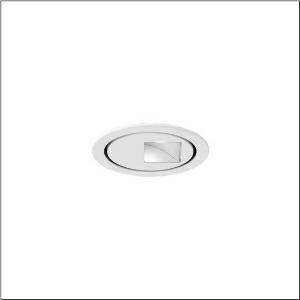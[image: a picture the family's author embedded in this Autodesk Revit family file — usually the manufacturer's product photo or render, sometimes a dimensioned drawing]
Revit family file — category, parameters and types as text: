
# Revit family: lunis_11_micro_round_51dj11b71wf21
name_source: partatom
category: Lighting Fixtures
units: mm (PartAtom-declared; Revit-internal decimal feet)

## family parameters
Cut with Voids When Loaded = No
Host = Face
Light Source = No
Part Type = Normal
Room Calculation Point = No
Round Connector Dimension = Use Diameter
Shared = No

## types (1)
- Lunis 11 micro round (1 x LED 3000K / CRI = 80 (unbekannt), 1320 lm, 3000K)
    Apparent Load = 20 VA
    CIE Flux Codes = 42 75 96 100 100
    Color Rendering = 80
    Color Temperature = 3000K
    Default Elevation = 1800 mm
    Description = Lunis 11 micro round, downlight, light control with wallwasher, of highly reflective aluminium, highly specular, light emission: direct distribution, LED rated luminous flux: 1.320lm, light colour: 830, control gear: ECG, with terminal, 3-pole, mains connection: 220..230V, AC/DC, 0/50..60Hz, LED module, luminaire module, of aluminium, highly specular, white, diameter: 114mm, clamping range: 1..40mm, recessing ring, of plastic, traffic white (RAL 9016), protection rating (complete): IP20, insulation class (complete): insulation class II (safety insulation), certification: CE, permissible ambient temperature for indoor applications: 0..+35°C, packaging unit: 1 piece
    Height = 0 mm  [stored 0 ft]
    Lamp = 1 x LED 3000K / CRI >= 80 (unbekannt)
    Lamp Light Flux = 1320 lm
    Lamp count = 1
    Length = 114 mm
    Luminous efficacy = 67 lm/W
    Manufacturer = Siteco
    ModVariant = No
    Model = 51DJ11B71WF21
    Mounting Place = Ceiling
    Mounting Type = Recessed
    Number of Poles = 1
    OnlyDefault = Yes
    Power Factor = 1
    Product Name = Lunis 11 micro round
    Product group = downlight | ceiling recessed
    ProductGroupID = 402
    Protection Class = Protection class II
    Protection Degree = IP 20
    RLX_Detail_Level = 1
    RlxData = <blob elided: 40881 chars, md5=af576269>
    Socket = socket
    Standby Power = 0 W
    System Light Flux = 1320 lm
    System Power = 20 W
    Type Comments = Product without accessories
    Type Image = l_1004773.jpg
    URL = http://relux.com
    VarID = ---
    Voltage = 0 V
    Weight = 0.00 kg
    Width = 114 mm

note: [stored X ft] marks values corroborated as IEEE doubles in the binary element streams (Revit-internal decimal feet)

## geometry (parser evidence)
native form markers: Blend x4, Sweep x10
no freeform markers — native parametric forms only
